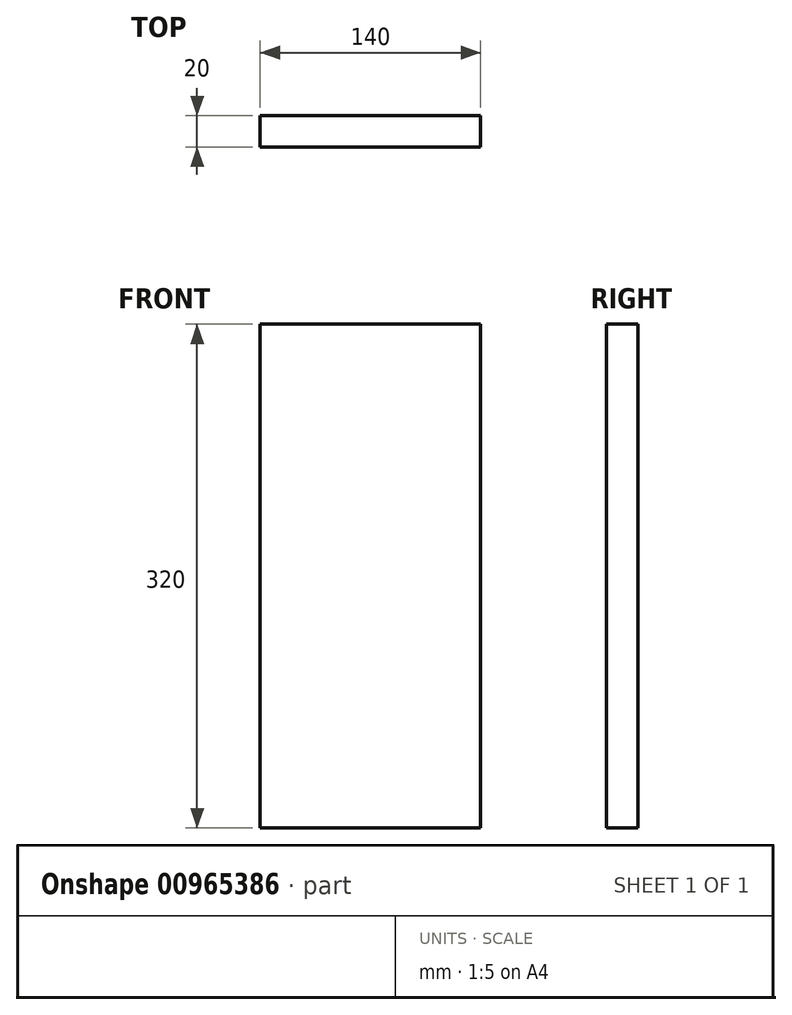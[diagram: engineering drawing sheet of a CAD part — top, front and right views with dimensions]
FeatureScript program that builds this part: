
annotation { "Feature Type Name" : "Feature", "Feature Type Description" : "" }
export const myFeature = defineFeature(function(context is Context, id is Id, definition is map)
    precondition{}
    {
        {
            var Q0;
            Q0=qCreatedBy(makeId("Top.planeOp"),FACE);
            var sketch = newSketch(context, id + "F0", { "sketchPlane" : qUnion([Q0])});
            skLineSegment(sketch, "E0.bottom", {"start": v(70, 10) * mm, "end": v(-70, 10) * mm});
            skLineSegment(sketch, "E0.top", {"start": v(70, -10) * mm, "end": v(-70, -10) * mm});
            skLineSegment(sketch, "E0.left", {"start": v(70, 10) * mm, "end": v(70, -10) * mm});
            skLineSegment(sketch, "E0.right", {"start": v(-70, 10) * mm, "end": v(-70, -10) * mm});
            skPoint(sketch, "E0.middle", {"position": v(0, 0) * mm});
            skSolve(sketch);
        }
        {
            var Q0;
            Q0=makeQuery(id+"F0.imprint","IMPRINT",FACE,{"disambiguationData":[TD([[makeQuery(id+"F0.imprint","IMPRINT",EDGE,{"derivedFrom":sQuery(id+"F0.wireOp",EDGE,"E0.bottom")}),1.0]])]});
            extrude(context, id + "F1", {"entities" : qUnion([Q0]), "depth" : 320 * mm, "offsetDistance" : 25 * mm});
        }
    });
